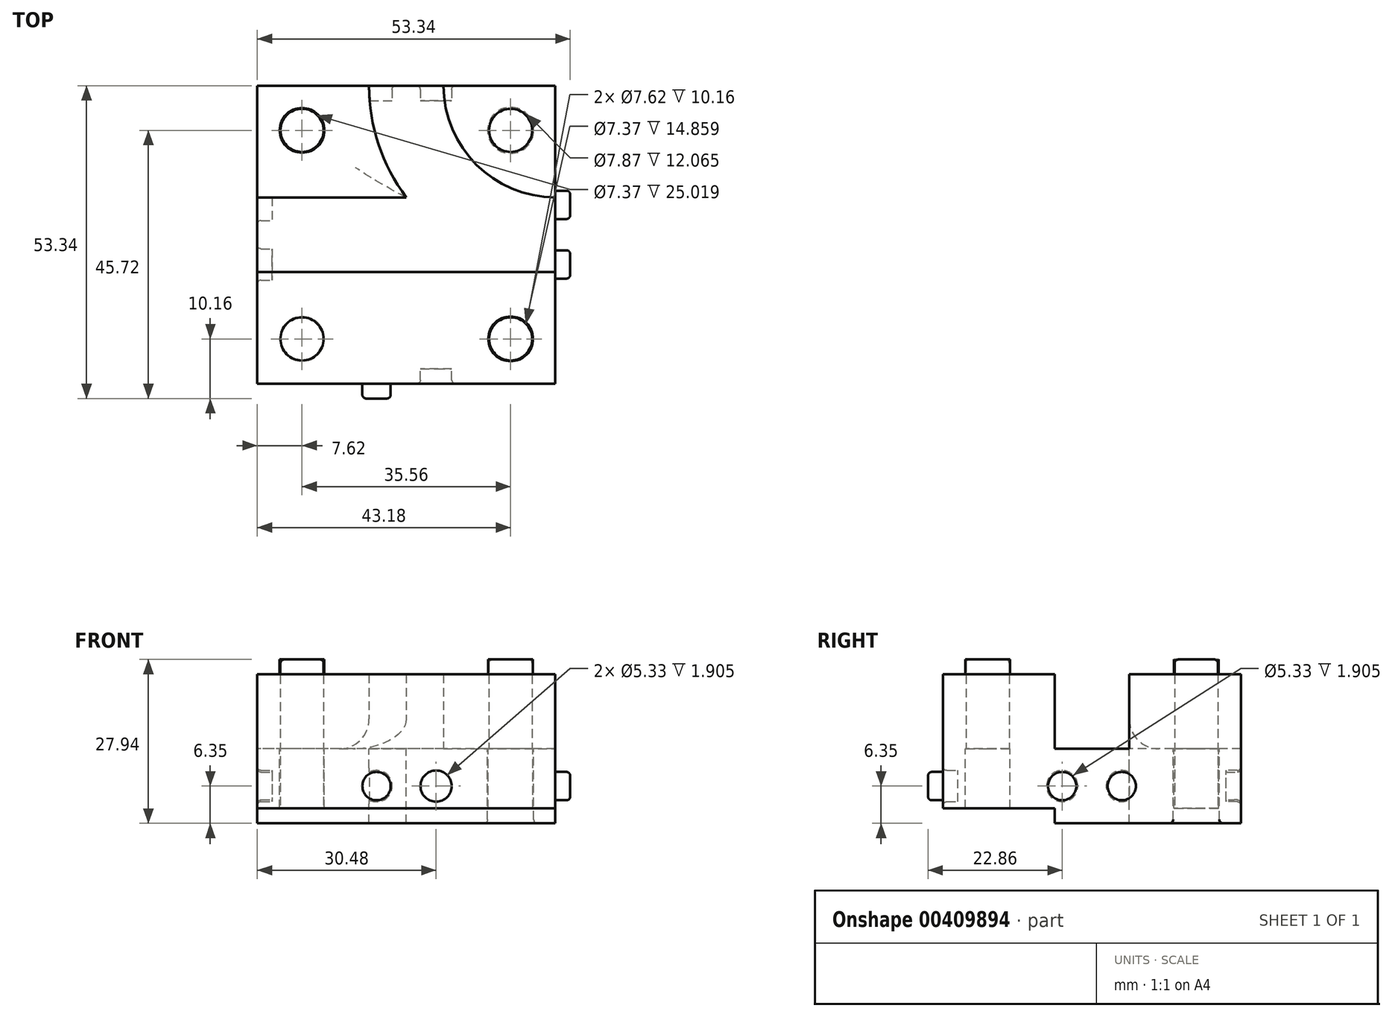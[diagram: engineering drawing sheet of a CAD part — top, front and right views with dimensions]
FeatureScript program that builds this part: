
annotation { "Feature Type Name" : "Feature", "Feature Type Description" : "" }
export const myFeature = defineFeature(function(context is Context, id is Id, definition is map)
    precondition{}
    {
        {
            var Q0;
            Q0=qCreatedBy(makeId("Top.planeOp"),FACE);
            var sketch = newSketch(context, id + "F0", { "sketchPlane" : qUnion([Q0])});
            skLineSegment(sketch, "E0.bottom", {"start": v(25.4, 25.4) * mm, "end": v(-25.4, 25.4) * mm});
            skLineSegment(sketch, "E0.top", {"start": v(25.4, -25.4) * mm, "end": v(-25.4, -25.4) * mm});
            skLineSegment(sketch, "E0.left", {"start": v(25.4, 25.4) * mm, "end": v(25.4, -25.4) * mm});
            skLineSegment(sketch, "E0.right", {"start": v(-25.4, 25.4) * mm, "end": v(-25.4, -25.4) * mm});
            skPoint(sketch, "E0.middle", {"position": v(0, 0) * mm});
            skPoint(sketch, "E1", {"position": v(17.78, 17.78) * mm});
            skCircle(sketch, "E2", {"center": v(17.78, 17.78) * mm, "radius": 3.81 * mm, "construction": true});
            skCircle(sketch, "E3.MirrorC", {"center": v(-17.78, 17.78) * mm, "radius": 3.81 * mm});
            skCircle(sketch, "E4.MirrorC", {"center": v(17.78, -17.78) * mm, "radius": 3.81 * mm});
            skCircle(sketch, "E5.MirrorC", {"center": v(-17.78, -17.78) * mm, "radius": 3.81 * mm});
            skPoint(sketch, "E6", {"position": v(25.4, 0) * mm});
            skPoint(sketch, "E7", {"position": v(-25.4, 0) * mm});
            skCircle(sketch, "E8", {"center": v(17.78, 17.78) * mm, "radius": 3.68 * mm});
            skCircle(sketch, "E9.MirrorC", {"center": v(-17.78, 17.78) * mm, "radius": 3.68 * mm});
            skCircle(sketch, "E10.MirrorC", {"center": v(-17.78, -17.78) * mm, "radius": 3.68 * mm});
            skCircle(sketch, "E11.MirrorC", {"center": v(17.78, -17.78) * mm, "radius": 3.68 * mm});
            skLineSegment(sketch, "E12", {"start": v(-25.4, 0) * mm, "end": v(25.4, 0) * mm, "construction": true});
            skPoint(sketch, "E13", {"position": v(6.35, 25.4) * mm});
            skPoint(sketch, "E14.MirrorP", {"position": v(-6.35, 25.4) * mm});
            skArc(sketch, "E15", {"start": v(6.35, 25.4) * mm, "mid": v(11.93, 11.93) * mm, "end": v(25.4, 6.35) * mm});
            skLineSegment(sketch, "E16", {"start": v(0, 25.4) * mm, "end": v(0, -25.4) * mm, "construction": true});
            skCircle(sketch, "E17", {"center": v(0, 0) * mm, "radius": 2.54 * mm, "construction": true});
            skPoint(sketch, "E18", {"position": v(0, 2.54) * mm});
            skPoint(sketch, "E19", {"position": v(0, 5.08) * mm});
            skCircle(sketch, "E20", {"center": v(0, 0) * mm, "radius": 2.41 * mm});
            skCircle(sketch, "E21", {"center": v(0, 0) * mm, "radius": 2.67 * mm});
            skPoint(sketch, "E22", {"position": v(2.41, 0) * mm});
            skPoint(sketch, "E23", {"position": v(2.67, 0) * mm});
            skLineSegment(sketch, "E24", {"start": v(2.41, 0) * mm, "end": v(2.67, 0) * mm});
            skCircle(sketch, "E25", {"center": v(17.78, 17.78) * mm, "radius": 3.94 * mm});
            skLineSegment(sketch, "E26", {"start": v(17.78, 21.46) * mm, "end": v(17.78, 21.72) * mm});
            skPoint(sketch, "E26.endSnap0", {"position": v(17.78, 21.59) * mm});
            skLineSegment(sketch, "E27", {"start": v(25.4, -6.35) * mm, "end": v(-25.4, -6.35) * mm});
            skLineSegment(sketch, "E28", {"start": v(25.4, 6.35) * mm, "end": v(0, 6.35) * mm, "construction": true});
            skLineSegment(sketch, "E29", {"start": v(0, 6.35) * mm, "end": v(-25.4, 6.35) * mm});
            skArc(sketch, "E30", {"start": v(-6.35, 25.4) * mm, "mid": v(-4.72, 15.36) * mm, "end": v(0, 6.35) * mm});
            skLineSegment(sketch, "E31", {"start": v(25.4, 6.35) * mm, "end": v(25.4, -6.35) * mm});
            skPoint(sketch, "E32", {"position": v(2.54, 0) * mm});
            skCircle(sketch, "E33", {"center": v(0, 0) * mm, "radius": 5.08 * mm});
            skLineSegment(sketch, "E34", {"start": v(17.78, 25.4) * mm, "end": v(17.78, 17.78) * mm, "construction": true});
            skLineSegment(sketch, "E35", {"start": v(17.78, 17.78) * mm, "end": v(25.4, 17.78) * mm, "construction": true});
            skSolve(sketch);
        }
        {
            var Q0;
            Q0=makeQuery(id+"F0.imprint","IMPRINT",FACE,{"disambiguationData":[TD([[makeQuery(id+"F0.imprint","IMPRINT",EDGE,{"derivedFrom":sQuery(id+"F0.wireOp",EDGE,"E3.MirrorC")}),1.0]])]});
            var Q1;
            {var subQ0=sQuery(id+"F0.wireOp",EDGE,"e8c6bd5a-b162-413f-9673-ee5317453a08.1.0");var subQ1=sQuery(id+"F0.wireOp",EDGE,"E0.right");var subQ2=makeQuery(id+"F0.imprint","INTERSECT",VERTEX,{"derivedFrom":[subQ1,subQ0]});Q1=makeQuery(id+"F0.imprint","IMPRINT",FACE,{"disambiguationData":[TD([[makeQuery(id+"F0.imprint","IMPRINT",EDGE,{"disambiguationData":[TD([[subQ2,-1.0]])],"derivedFrom":subQ1}),1.0]])]});}
            var Q2;
            Q2=makeQuery(id+"F0.imprint","IMPRINT",FACE,{"disambiguationData":[TD([[makeQuery(id+"F0.imprint","IMPRINT",EDGE,{"derivedFrom":sQuery(id+"F0.wireOp",EDGE,"E5.MirrorC")}),-1.0]])]});
            var Q3;
            Q3=makeQuery(id+"F0.imprint","IMPRINT",FACE,{"disambiguationData":[TD([[makeQuery(id+"F0.imprint","IMPRINT",EDGE,{"derivedFrom":sQuery(id+"F0.wireOp",EDGE,"E3.MirrorC")}),-1.0]])]});
            var Q4;
            Q4=makeQuery(id+"F0.imprint","IMPRINT",FACE,{"disambiguationData":[TD([[makeQuery(id+"F0.imprint","IMPRINT",EDGE,{"derivedFrom":sQuery(id+"F0.wireOp",EDGE,"E5.MirrorC")}),1.0]])]});
            var Q5;
            Q5=makeQuery(id+"F0.imprint","IMPRINT",FACE,{"disambiguationData":[TD([[makeQuery(id+"F0.imprint","IMPRINT",EDGE,{"derivedFrom":sQuery(id+"F0.wireOp",EDGE,"E4.MirrorC")}),-1.0]])]});
            var Q6;
            {var subQ0=sQuery(id+"F0.wireOp",EDGE,"E16");var subQ1=sQuery(id+"F0.wireOp",EDGE,"E0.top");var subQ2=makeQuery(id+"F0.imprint","INTERSECT",VERTEX,{"derivedFrom":[subQ1,subQ0]});Q6=makeQuery(id+"F0.imprint","IMPRINT",FACE,{"disambiguationData":[TD([[makeQuery(id+"F0.imprint","IMPRINT",EDGE,{"disambiguationData":[TD([[subQ2,-1.0]])],"derivedFrom":subQ1}),-1.0]])]});}
            var Q7;
            {var subQ0=sQuery(id+"F0.wireOp",EDGE,"E16");var subQ1=sQuery(id+"F0.wireOp",EDGE,"E0.top");var subQ2=makeQuery(id+"F0.imprint","INTERSECT",VERTEX,{"derivedFrom":[subQ1,subQ0]});Q7=makeQuery(id+"F0.imprint","IMPRINT",FACE,{"disambiguationData":[TD([[makeQuery(id+"F0.imprint","IMPRINT",EDGE,{"disambiguationData":[TD([[subQ2,1.0]])],"derivedFrom":subQ1}),-1.0]])]});}
            var Q8;
            Q8=makeQuery(id+"F0.imprint","IMPRINT",FACE,{"disambiguationData":[TD([[makeQuery(id+"F0.imprint","IMPRINT",EDGE,{"derivedFrom":sQuery(id+"F0.wireOp",EDGE,"E4.MirrorC")}),1.0]])]});
            var Q9;
            Q9=makeQuery(id+"F0.imprint","IMPRINT",FACE,{"disambiguationData":[TD([[makeQuery(id+"F0.imprint","IMPRINT",EDGE,{"derivedFrom":sQuery(id+"F0.wireOp",EDGE,"E8")}),-1.0]])]});
            var Q10;
            {var subQ5=sQuery(id+"F0.wireOp",EDGE,"E15");Q10=makeQuery(id+"F0.imprint","IMPRINT",FACE,{"disambiguationData":[TD([[makeQuery(id+"F0.imprint","IMPRINT",EDGE,{"derivedFrom":subQ5}),1.0]])]});}
            var Q11;
            {var subQ0=sQuery(id+"F0.wireOp",EDGE,"E34");var subQ1=sQuery(id+"F0.wireOp",EDGE,"E8");var subQ2=makeQuery(id+"F0.imprint","INTERSECT",VERTEX,{"derivedFrom":[subQ1,subQ0]});Q11=makeQuery(id+"F0.imprint","IMPRINT",FACE,{"disambiguationData":[TD([[makeQuery(id+"F0.imprint","IMPRINT",EDGE,{"disambiguationData":[TD([[subQ2,1.0]])],"derivedFrom":subQ1}),1.0]])]});}
            var Q12;
            {var subQ0=sQuery(id+"F0.wireOp",EDGE,"E34");var subQ1=sQuery(id+"F0.wireOp",EDGE,"E8");var subQ2=makeQuery(id+"F0.imprint","INTERSECT",VERTEX,{"derivedFrom":[subQ1,subQ0]});Q12=makeQuery(id+"F0.imprint","IMPRINT",FACE,{"disambiguationData":[TD([[makeQuery(id+"F0.imprint","IMPRINT",EDGE,{"disambiguationData":[TD([[subQ2,-1.0]])],"derivedFrom":subQ1}),1.0]])]});}
            var Q13;
            Q13=makeQuery(id+"F0.imprint","IMPRINT",FACE,{"disambiguationData":[TD([[makeQuery(id+"F0.imprint","IMPRINT",EDGE,{"derivedFrom":sQuery(id+"F0.wireOp",EDGE,"E9.MirrorC")}),-1.0]])]});
            var Q14;
            Q14=makeQuery(id+"F0.imprint","IMPRINT",FACE,{"disambiguationData":[TD([[makeQuery(id+"F0.imprint","IMPRINT",EDGE,{"derivedFrom":sQuery(id+"F0.wireOp",EDGE,"E10.MirrorC")}),1.0]])]});
            var Q15;
            Q15=makeQuery(id+"F0.imprint","IMPRINT",FACE,{"disambiguationData":[TD([[makeQuery(id+"F0.imprint","IMPRINT",EDGE,{"derivedFrom":sQuery(id+"F0.wireOp",EDGE,"E11.MirrorC")}),-1.0]])]});
            extrude(context, id + "F1", {"entities" : qUnion([Q0, Q1, Q2, Q3, Q4, Q5, Q6, Q7, Q8, Q9, Q10, Q11, Q12, Q13, Q14, Q15]), "depth" : 12.7 * mm});
        }
        {
            var Q0;
            Q0=makeQuery(id+"F0.imprint","IMPRINT",FACE,{"disambiguationData":[TD([[makeQuery(id+"F0.imprint","IMPRINT",EDGE,{"derivedFrom":sQuery(id+"F0.wireOp",EDGE,"E10.MirrorC")}),1.0]])]});
            var Q1;
            Q1=makeQuery(id+"F0.imprint","IMPRINT",FACE,{"disambiguationData":[TD([[makeQuery(id+"F0.imprint","IMPRINT",EDGE,{"derivedFrom":sQuery(id+"F0.wireOp",EDGE,"E9.MirrorC")}),-1.0]])]});
            var Q2;
            Q2=makeQuery(id+"F0.imprint","IMPRINT",FACE,{"disambiguationData":[TD([[makeQuery(id+"F0.imprint","IMPRINT",EDGE,{"derivedFrom":sQuery(id+"F0.wireOp",EDGE,"E8")}),1.0]])]});
            var Q3;
            Q3=makeQuery(id+"F0.imprint","IMPRINT",FACE,{"disambiguationData":[TD([[makeQuery(id+"F0.imprint","IMPRINT",EDGE,{"derivedFrom":sQuery(id+"F0.wireOp",EDGE,"E11.MirrorC")}),-1.0]])]});
            extrude(context, id + "F2", {"entities" : qUnion([Q0, Q1, Q2, Q3]), "operationType" : NewBodyOperationType.ADD, "depth" : 15.24 * mm});
        }
        {
            var Q0;
            {var subQ0=sQuery(id+"F0.wireOp",EDGE,"e8c6bd5a-b162-413f-9673-ee5317453a08.1.0");var subQ1=sQuery(id+"F0.wireOp",EDGE,"E0.left");var subQ2=makeQuery(id+"F0.imprint","INTERSECT",VERTEX,{"derivedFrom":[subQ1,subQ0]});Q0=makeQuery(id+"F0.imprint","IMPRINT",FACE,{"disambiguationData":[TD([[makeQuery(id+"F0.imprint","IMPRINT",EDGE,{"disambiguationData":[TD([[subQ2,-1.0]])],"derivedFrom":subQ1}),-1.0]])]});}
            var Q1;
            {var subQ0=sQuery(id+"F0.wireOp",EDGE,"abd07589-5baa-48c3-989b-ebb05b9b5cfd");var subQ1=sQuery(id+"F0.wireOp",EDGE,"E0.bottom");var subQ2=makeQuery(id+"F0.imprint","INTERSECT",VERTEX,{"derivedFrom":[subQ1,subQ0]});Q1=makeQuery(id+"F0.imprint","IMPRINT",FACE,{"disambiguationData":[TD([[makeQuery(id+"F0.imprint","IMPRINT",EDGE,{"disambiguationData":[TD([[subQ2,1.0]])],"derivedFrom":subQ1}),1.0]])]});}
            var Q2;
            {var subQ0=sQuery(id+"F0.wireOp",EDGE,"E16");var subQ1=sQuery(id+"F0.wireOp",EDGE,"E0.bottom");var subQ2=makeQuery(id+"F0.imprint","INTERSECT",VERTEX,{"derivedFrom":[subQ1,subQ0]});Q2=makeQuery(id+"F0.imprint","IMPRINT",FACE,{"disambiguationData":[TD([[makeQuery(id+"F0.imprint","IMPRINT",EDGE,{"disambiguationData":[TD([[subQ2,-1.0]])],"derivedFrom":subQ1}),1.0]])]});}
            var Q3;
            {var subQ0=sQuery(id+"F0.wireOp",EDGE,"E16");var subQ1=sQuery(id+"F0.wireOp",EDGE,"E0.bottom");var subQ2=makeQuery(id+"F0.imprint","INTERSECT",VERTEX,{"derivedFrom":[subQ1,subQ0]});Q3=makeQuery(id+"F0.imprint","IMPRINT",FACE,{"disambiguationData":[TD([[makeQuery(id+"F0.imprint","IMPRINT",EDGE,{"disambiguationData":[TD([[subQ2,1.0]])],"derivedFrom":subQ1}),1.0]])]});}
            var Q4;
            {var subQ5=sQuery(id+"F0.wireOp",EDGE,"E15");Q4=makeQuery(id+"F0.imprint","IMPRINT",FACE,{"disambiguationData":[TD([[makeQuery(id+"F0.imprint","IMPRINT",EDGE,{"derivedFrom":subQ5}),-1.0]])]});}
            var Q5;
            {var subQ0=sQuery(id+"F0.wireOp",EDGE,"E12");var subQ1=sQuery(id+"F0.wireOp",EDGE,"E0.left");var subQ2=makeQuery(id+"F0.imprint","INTERSECT",VERTEX,{"derivedFrom":[subQ1,subQ0]});Q5=makeQuery(id+"F0.imprint","IMPRINT",FACE,{"disambiguationData":[TD([[makeQuery(id+"F0.imprint","IMPRINT",EDGE,{"disambiguationData":[TD([[subQ2,1.0]])],"derivedFrom":subQ1}),-1.0]])]});}
            var Q6;
            {var subQ1=sQuery(id+"F0.wireOp",EDGE,"E12");var subQ7=sQuery(id+"F0.wireOp",EDGE,"E0.left");var subQ8=makeQuery(id+"F0.imprint","INTERSECT",VERTEX,{"derivedFrom":[subQ7,subQ1]});Q6=makeQuery(id+"F0.imprint","IMPRINT",FACE,{"disambiguationData":[TD([[makeQuery(id+"F0.imprint","IMPRINT",EDGE,{"disambiguationData":[TD([[subQ8,-1.0]])],"derivedFrom":subQ7}),-1.0]])]});}
            var Q7;
            Q7=makeQuery(id+"F0.imprint","IMPRINT",FACE,{"disambiguationData":[TD([[makeQuery(id+"F0.imprint","IMPRINT",EDGE,{"derivedFrom":sQuery(id+"F0.wireOp",EDGE,"E20")}),1.0]])]});
            var Q8;
            Q8=makeQuery(id+"F0.imprint","IMPRINT",FACE,{"disambiguationData":[TD([[makeQuery(id+"F0.imprint","IMPRINT",EDGE,{"derivedFrom":sQuery(id+"F0.wireOp",EDGE,"E20")}),-1.0]])]});
            var Q9;
            {var subQ11=sQuery(id+"F0.wireOp",EDGE,"E0.top");Q9=makeQuery(id+"F0.imprint","IMPRINT",FACE,{"disambiguationData":[TD([[makeQuery(id+"F0.imprint","IMPRINT",EDGE,{"derivedFrom":subQ11}),-1.0]])]});}
            var Q10;
            Q10=makeQuery(id+"F0.imprint","IMPRINT",FACE,{"disambiguationData":[TD([[makeQuery(id+"F0.imprint","IMPRINT",EDGE,{"derivedFrom":sQuery(id+"F0.wireOp",EDGE,"E3.MirrorC")}),1.0]])]});
            var Q11;
            Q11=makeQuery(id+"F0.imprint","IMPRINT",FACE,{"disambiguationData":[TD([[makeQuery(id+"F0.imprint","IMPRINT",EDGE,{"derivedFrom":sQuery(id+"F0.wireOp",EDGE,"E21")}),-1.0]])]});
            extrude(context, id + "F3", {"entities" : qUnion([Q0, Q1, Q2, Q3, Q4, Q5, Q6, Q7, Q8, Q9, Q10, Q11]), "operationType" : NewBodyOperationType.ADD, "oppositeDirection" : true, "depth" : 12.7 * mm});
        }
        {
            var Q0;
            Q0=makeQuery(id+"F0.imprint","IMPRINT",FACE,{"disambiguationData":[TD([[makeQuery(id+"F0.imprint","IMPRINT",EDGE,{"derivedFrom":sQuery(id+"F0.wireOp",EDGE,"E11.MirrorC")}),-1.0]])]});
            var Q1;
            Q1=makeQuery(id+"F0.imprint","IMPRINT",FACE,{"disambiguationData":[TD([[makeQuery(id+"F0.imprint","IMPRINT",EDGE,{"derivedFrom":sQuery(id+"F0.wireOp",EDGE,"E5.MirrorC")}),1.0]])]});
            var Q2;
            Q2=makeQuery(id+"F0.imprint","IMPRINT",FACE,{"disambiguationData":[TD([[makeQuery(id+"F0.imprint","IMPRINT",EDGE,{"derivedFrom":sQuery(id+"F0.wireOp",EDGE,"E10.MirrorC")}),1.0]])]});
            var Q3;
            Q3=makeQuery(id+"F0.imprint","IMPRINT",FACE,{"disambiguationData":[TD([[makeQuery(id+"F0.imprint","IMPRINT",EDGE,{"derivedFrom":sQuery(id+"F0.wireOp",EDGE,"E4.MirrorC")}),-1.0]])]});
            var Q4;
            Q4=makeQuery(id+"F0.imprint","IMPRINT",FACE,{"disambiguationData":[TD([[makeQuery(id+"F0.imprint","IMPRINT",EDGE,{"derivedFrom":sQuery(id+"F0.wireOp",EDGE,"E8")}),-1.0]])]});
            var Q5;
            Q5=makeQuery(id+"F0.imprint","IMPRINT",FACE,{"disambiguationData":[TD([[makeQuery(id+"F0.imprint","IMPRINT",EDGE,{"derivedFrom":sQuery(id+"F0.wireOp",EDGE,"E8")}),1.0]])]});
            var Q6;
            Q6=makeQuery(id+"F0.imprint","IMPRINT",FACE,{"disambiguationData":[TD([[makeQuery(id+"F0.imprint","IMPRINT",EDGE,{"derivedFrom":sQuery(id+"F0.wireOp",EDGE,"E3.MirrorC")}),-1.0]])]});
            var Q7;
            Q7=makeQuery(id+"F0.imprint","IMPRINT",FACE,{"disambiguationData":[TD([[makeQuery(id+"F0.imprint","IMPRINT",EDGE,{"derivedFrom":sQuery(id+"F0.wireOp",EDGE,"E9.MirrorC")}),-1.0]])]});
            extrude(context, id + "F4", {"entities" : qUnion([Q0, Q1, Q2, Q3, Q4, Q5, Q6, Q7]), "operationType" : NewBodyOperationType.REMOVE, "oppositeDirection" : true, "depth" : 12.7 * mm, "hasSecondDirection" : true, "secondDirectionOppositeDirection" : true, "secondDirectionDepth" : 10.16 * mm});
        }
        {
            var Q0;
            Q0=qCreatedBy(makeId("Right.planeOp"),FACE);
            var sketch = newSketch(context, id + "F5", { "sketchPlane" : qUnion([Q0])});
            skLineSegment(sketch, "E36", {"start": v(-25.4, 12.7) * mm, "end": v(-25.4, -12.7) * mm, "construction": true});
            skLineSegment(sketch, "E37", {"start": v(25.4, 0) * mm, "end": v(25.4, -12.7) * mm, "construction": true});
            skPoint(sketch, "E38", {"position": v(-25.4, 0) * mm});
            skPoint(sketch, "E39", {"position": v(-25.4, -6.35) * mm});
            skPoint(sketch, "E40", {"position": v(25.4, -6.35) * mm});
            skLineSegment(sketch, "E41", {"start": v(-2.41, 0) * mm, "end": v(-2.67, 0) * mm, "construction": true});
            skLineSegment(sketch, "E42", {"start": v(2.67, 0) * mm, "end": v(2.41, 0) * mm, "construction": true});
            skPoint(sketch, "E43", {"position": v(-5.08, -6.35) * mm});
            skPoint(sketch, "E44", {"position": v(-2.67, -6.35) * mm});
            skPoint(sketch, "E45", {"position": v(-2.41, -6.35) * mm});
            skPoint(sketch, "E46", {"position": v(2.41, -6.35) * mm});
            skPoint(sketch, "E47", {"position": v(2.67, -6.35) * mm});
            skPoint(sketch, "E48", {"position": v(5.08, -6.35) * mm});
            skCircle(sketch, "E49", {"center": v(-5.08, -6.35) * mm, "radius": 2.41 * mm});
            skCircle(sketch, "E50", {"center": v(-5.08, -6.35) * mm, "radius": 2.67 * mm});
            skCircle(sketch, "E51", {"center": v(5.08, -6.35) * mm, "radius": 2.41 * mm});
            skCircle(sketch, "E52", {"center": v(5.08, -6.35) * mm, "radius": 2.67 * mm});
            skLineSegment(sketch, "E53", {"start": v(-2.67, 0) * mm, "end": v(-5.08, 0) * mm});
            skLineSegment(sketch, "E54", {"start": v(5.08, 0) * mm, "end": v(2.67, 0) * mm});
            skSolve(sketch);
        }
        {
            var Q0;
            Q0=qCreatedBy(makeId("Front.planeOp"),FACE);
            var sketch = newSketch(context, id + "F6", { "sketchPlane" : qUnion([Q0])});
            skLineSegment(sketch, "E55", {"start": v(-25.4, -12.7) * mm, "end": v(-25.4, 12.7) * mm, "construction": true});
            skLineSegment(sketch, "E56", {"start": v(25.4, -12.7) * mm, "end": v(25.4, 0) * mm, "construction": true});
            skPoint(sketch, "E57", {"position": v(25.4, -6.35) * mm});
            skPoint(sketch, "E58", {"position": v(-25.4, 0) * mm});
            skPoint(sketch, "E59", {"position": v(-25.4, -6.35) * mm});
            skLineSegment(sketch, "E60", {"start": v(-2.41, 0) * mm, "end": v(-2.67, 0) * mm, "construction": true});
            skLineSegment(sketch, "E61", {"start": v(2.67, 0) * mm, "end": v(2.41, 0) * mm, "construction": true});
            skPoint(sketch, "E62", {"position": v(5.08, -6.35) * mm});
            skPoint(sketch, "E63", {"position": v(2.67, -6.35) * mm});
            skPoint(sketch, "E64", {"position": v(2.41, -6.35) * mm});
            skPoint(sketch, "E65", {"position": v(-2.41, -6.35) * mm});
            skPoint(sketch, "E66", {"position": v(-2.67, -6.35) * mm});
            skPoint(sketch, "E67", {"position": v(-5.08, -6.35) * mm});
            skCircle(sketch, "E68", {"center": v(5.08, -6.35) * mm, "radius": 2.41 * mm});
            skCircle(sketch, "E69", {"center": v(5.08, -6.35) * mm, "radius": 2.67 * mm});
            skCircle(sketch, "E70", {"center": v(-5.08, -6.35) * mm, "radius": 2.67 * mm});
            skCircle(sketch, "E71", {"center": v(-5.08, -6.35) * mm, "radius": 2.41 * mm});
            skLineSegment(sketch, "E72", {"start": v(-2.67, 0) * mm, "end": v(-5.08, 0) * mm});
            skLineSegment(sketch, "E73", {"start": v(5.08, 0) * mm, "end": v(2.67, 0) * mm});
            skSolve(sketch);
        }
        {
            var Q0;
            Q0=makeQuery(id+"F6.imprint","IMPRINT",FACE,{"disambiguationData":[TD([[makeQuery(id+"F6.imprint","IMPRINT",EDGE,{"derivedFrom":sQuery(id+"F6.wireOp",EDGE,"E71")}),1.0]])]});
            extrude(context, id + "F7", {"entities" : qUnion([Q0]), "operationType" : NewBodyOperationType.ADD, "depth" : 27.94 * mm, "hasSecondDirection" : true, "secondDirectionOppositeDirection" : false, "secondDirectionDepth" : 22.86 * mm});
        }
        {
            var Q0;
            Q0=makeQuery(id+"F6.imprint","IMPRINT",FACE,{"disambiguationData":[TD([[makeQuery(id+"F6.imprint","IMPRINT",EDGE,{"derivedFrom":sQuery(id+"F6.wireOp",EDGE,"E71")}),1.0]])]});
            var Q1;
            Q1=makeQuery(id+"F6.imprint","IMPRINT",FACE,{"disambiguationData":[TD([[makeQuery(id+"F6.imprint","IMPRINT",EDGE,{"derivedFrom":sQuery(id+"F6.wireOp",EDGE,"E68")}),1.0]])]});
            var Q2;
            Q2=makeQuery(id+"F6.imprint","IMPRINT",FACE,{"disambiguationData":[TD([[makeQuery(id+"F6.imprint","IMPRINT",EDGE,{"derivedFrom":sQuery(id+"F6.wireOp",EDGE,"E70")}),1.0]])]});
            var Q3;
            Q3=makeQuery(id+"F6.imprint","IMPRINT",FACE,{"disambiguationData":[TD([[makeQuery(id+"F6.imprint","IMPRINT",EDGE,{"derivedFrom":sQuery(id+"F6.wireOp",EDGE,"E68")}),-1.0]])]});
            extrude(context, id + "F8", {"entities" : qUnion([Q0, Q1, Q2, Q3]), "operationType" : NewBodyOperationType.REMOVE, "oppositeDirection" : true, "depth" : 27.94 * mm, "hasSecondDirection" : true, "secondDirectionOppositeDirection" : true, "secondDirectionDepth" : 22.86 * mm});
        }
        {
            var Q0;
            Q0=makeQuery(id+"F5.imprint","IMPRINT",FACE,{"disambiguationData":[TD([[makeQuery(id+"F5.imprint","IMPRINT",EDGE,{"derivedFrom":sQuery(id+"F5.wireOp",EDGE,"E49")}),1.0]])]});
            var Q1;
            Q1=makeQuery(id+"F5.imprint","IMPRINT",FACE,{"disambiguationData":[TD([[makeQuery(id+"F5.imprint","IMPRINT",EDGE,{"derivedFrom":sQuery(id+"F5.wireOp",EDGE,"E51")}),1.0]])]});
            extrude(context, id + "F9", {"entities" : qUnion([Q0, Q1]), "operationType" : NewBodyOperationType.ADD, "depth" : 27.94 * mm, "hasSecondDirection" : true, "secondDirectionOppositeDirection" : false, "secondDirectionDepth" : 22.86 * mm});
        }
        {
            var Q0;
            Q0=makeQuery(id+"F5.imprint","IMPRINT",FACE,{"disambiguationData":[TD([[makeQuery(id+"F5.imprint","IMPRINT",EDGE,{"derivedFrom":sQuery(id+"F5.wireOp",EDGE,"E49")}),-1.0]])]});
            var Q1;
            Q1=makeQuery(id+"F5.imprint","IMPRINT",FACE,{"disambiguationData":[TD([[makeQuery(id+"F5.imprint","IMPRINT",EDGE,{"derivedFrom":sQuery(id+"F5.wireOp",EDGE,"E49")}),1.0]])]});
            var Q2;
            Q2=makeQuery(id+"F5.imprint","IMPRINT",FACE,{"disambiguationData":[TD([[makeQuery(id+"F5.imprint","IMPRINT",EDGE,{"derivedFrom":sQuery(id+"F5.wireOp",EDGE,"E51")}),1.0]])]});
            var Q3;
            Q3=makeQuery(id+"F5.imprint","IMPRINT",FACE,{"disambiguationData":[TD([[makeQuery(id+"F5.imprint","IMPRINT",EDGE,{"derivedFrom":sQuery(id+"F5.wireOp",EDGE,"E51")}),-1.0]])]});
            extrude(context, id + "F10", {"entities" : qUnion([Q0, Q1, Q2, Q3]), "operationType" : NewBodyOperationType.REMOVE, "oppositeDirection" : true, "depth" : 27.94 * mm, "hasSecondDirection" : true, "secondDirectionOppositeDirection" : true, "secondDirectionDepth" : 22.86 * mm});
        }
        {
            var Q0;
            Q0=makeQuery(id+"F6.imprint","IMPRINT",FACE,{"disambiguationData":[TD([[makeQuery(id+"F6.imprint","IMPRINT",EDGE,{"derivedFrom":sQuery(id+"F6.wireOp",EDGE,"E68")}),1.0]])]});
            var Q1;
            Q1=makeQuery(id+"F6.imprint","IMPRINT",FACE,{"disambiguationData":[TD([[makeQuery(id+"F6.imprint","IMPRINT",EDGE,{"derivedFrom":sQuery(id+"F6.wireOp",EDGE,"E68")}),-1.0]])]});
            extrude(context, id + "F11", {"entities" : qUnion([Q0, Q1]), "operationType" : NewBodyOperationType.REMOVE, "depth" : 27.94 * mm, "hasSecondDirection" : true, "secondDirectionOppositeDirection" : false, "secondDirectionDepth" : 22.86 * mm});
        }
        {
            var Q0;
            Q0=makeQuery(id+"F1.opExtrude","CAP_EDGE",EDGE,{"disambiguationData":[OSD([sQuery(id+"F0.wireOp",EDGE,"E15")])],"isStart":true});
            var Q1;
            Q1=makeQuery(id+"F1.opExtrude","CAP_EDGE",EDGE,{"disambiguationData":[OSD([sQuery(id+"F0.wireOp",EDGE,"E30")])],"isStart":true});
            var Q2;
            Q2=makeQuery(id+"F1.opExtrude","CAP_EDGE",EDGE,{"disambiguationData":[OSD([sQuery(id+"F0.wireOp",EDGE,"E27")])],"isStart":true});
            var Q3;
            Q3=makeQuery(id+"F1.opExtrude","CAP_EDGE",EDGE,{"disambiguationData":[OSD([sQuery(id+"F0.wireOp",EDGE,"E29")])],"isStart":true});
            fillet(context, id + "F12", {"entities" : qUnion([Q0, Q1, Q2, Q3]), "radius" : 5.08 * mm, "tangentPropagation" : true, "allowEdgeOverflow" : false});
        }
        {
            var Q0;
            Q0=makeQuery(id+"F2.opExtrude","CAP_EDGE",EDGE,{"disambiguationData":[OSD([sQuery(id+"F0.wireOp",EDGE,"E11.MirrorC")])],"isStart":false});
            var Q1;
            Q1=makeQuery(id+"F2.opExtrude","CAP_EDGE",EDGE,{"disambiguationData":[OSD([sQuery(id+"F0.wireOp",EDGE,"E10.MirrorC")])],"isStart":false});
            var Q2;
            Q2=makeQuery(id+"F2.opExtrude","CAP_EDGE",EDGE,{"disambiguationData":[OSD([sQuery(id+"F0.wireOp",EDGE,"E9.MirrorC")])],"isStart":false});
            var Q3;
            Q3=makeQuery(id+"F2.opExtrude","CAP_EDGE",EDGE,{"disambiguationData":[OSD([sQuery(id+"F0.wireOp",EDGE,"E8")])],"isStart":false});
            var Q4;
            Q4=makeQuery(id+"F7.opExtrude","CAP_EDGE",EDGE,{"disambiguationData":[OSD([sQuery(id+"F6.wireOp",EDGE,"E71")])],"isStart":false});
            var Q5;
            Q5=makeQuery(id+"F3.opExtrude","CAP_EDGE",EDGE,{"disambiguationData":[OSD([sQuery(id+"F0.wireOp",EDGE,"E5.MirrorC")])],"isStart":false});
            var Q6;
            Q6=makeQuery(id+"F3.opExtrude","CAP_EDGE",EDGE,{"disambiguationData":[OSD([sQuery(id+"F0.wireOp",EDGE,"E4.MirrorC")])],"isStart":false});
            var Q7;
            Q7=makeQuery(id+"F4.opExtrude","CAP_EDGE",EDGE,{"disambiguationData":[OSD([sQuery(id+"F0.wireOp",EDGE,"E3.MirrorC")])],"isStart":false});
            var Q8;
            Q8=makeQuery(id+"F3.opExtrude","CAP_EDGE",EDGE,{"disambiguationData":[OSD([sQuery(id+"F0.wireOp",EDGE,"E25")])],"isStart":false});
            var Q9;
            {var subQ0=sQuery(id+"F0.wireOp",EDGE,"E0.right");Q9=makeQuery(id+"F10.boolean.opBoolean","INTERSECT",EDGE,{"derivedFrom":[makeQuery(id+"FVeaqIvGeaTVGBi_11.opBoolean","MERGE",FACE,{"derivedFrom":[makeQuery(id+"F1.opExtrude","SWEPT_FACE",FACE,{"disambiguationData":[OSD([subQ0])]}),makeQuery(id+"F3.opExtrude","SWEPT_FACE",FACE,{"disambiguationData":[OSD([subQ0])]})]}),makeQuery(id+"F10.opExtrude","SWEPT_FACE",FACE,{"disambiguationData":[OSD([sQuery(id+"F5.wireOp",EDGE,"E50")])]})]});}
            var Q10;
            {var subQ0=sQuery(id+"F0.wireOp",EDGE,"E0.top");Q10=makeQuery(id+"F11.boolean.opBoolean","INTERSECT",EDGE,{"derivedFrom":[makeQuery(id+"FVeaqIvGeaTVGBi_11.opBoolean","MERGE",FACE,{"derivedFrom":[makeQuery(id+"F1.opExtrude","SWEPT_FACE",FACE,{"disambiguationData":[OSD([subQ0])]}),makeQuery(id+"F3.opExtrude","SWEPT_FACE",FACE,{"disambiguationData":[OSD([subQ0])]})]}),makeQuery(id+"F11.opExtrude","SWEPT_FACE",FACE,{"disambiguationData":[OSD([sQuery(id+"F6.wireOp",EDGE,"E69")])]})]});}
            var Q11;
            Q11=makeQuery(id+"F9.opExtrude","CAP_EDGE",EDGE,{"disambiguationData":[OSD([sQuery(id+"F5.wireOp",EDGE,"E51")])],"isStart":false});
            var Q12;
            Q12=makeQuery(id+"F9.opExtrude","CAP_EDGE",EDGE,{"disambiguationData":[OSD([sQuery(id+"F5.wireOp",EDGE,"E49")])],"isStart":false});
            var Q13;
            {var subQ0=sQuery(id+"F0.wireOp",EDGE,"lMXQf7WU-VQvn-eUw7-3v8j-XpuHpQXpMMjl");var subQ1=sQuery(id+"F0.wireOp",EDGE,"E0.bottom");Q13=makeQuery(id+"F8.boolean.opBoolean","INTERSECT",EDGE,{"derivedFrom":[makeQuery(id+"FVeaqIvGeaTVGBi_11.opBoolean","MERGE",FACE,{"derivedFrom":[makeQuery(id+"F1.opExtrude","SWEPT_FACE",FACE,{"disambiguationData":[OSD([subQ1,subQ0])]}),makeQuery(id+"F1.opExtrude","SWEPT_FACE",FACE,{"disambiguationData":[OSD([subQ1])]}),makeQuery(id+"F3.opExtrude","SWEPT_FACE",FACE,{"disambiguationData":[OSD([subQ1,subQ0])]})]}),makeQuery(id+"F8.opExtrude","SWEPT_FACE",FACE,{"disambiguationData":[OSD([sQuery(id+"F6.wireOp",EDGE,"E69")])]})]});}
            var Q14;
            {var subQ0=sQuery(id+"F0.wireOp",EDGE,"lMXQf7WU-VQvn-eUw7-3v8j-XpuHpQXpMMjl");var subQ1=sQuery(id+"F0.wireOp",EDGE,"E0.bottom");Q14=makeQuery(id+"F8.boolean.opBoolean","INTERSECT",EDGE,{"derivedFrom":[makeQuery(id+"FVeaqIvGeaTVGBi_11.opBoolean","MERGE",FACE,{"derivedFrom":[makeQuery(id+"F1.opExtrude","SWEPT_FACE",FACE,{"disambiguationData":[OSD([subQ1,subQ0])]}),makeQuery(id+"F1.opExtrude","SWEPT_FACE",FACE,{"disambiguationData":[OSD([subQ1])]}),makeQuery(id+"F3.opExtrude","SWEPT_FACE",FACE,{"disambiguationData":[OSD([subQ1,subQ0])]})]}),makeQuery(id+"F8.opExtrude","SWEPT_FACE",FACE,{"disambiguationData":[OSD([sQuery(id+"F6.wireOp",EDGE,"E70")])]})]});}
            var Q15;
            {var subQ0=sQuery(id+"F0.wireOp",EDGE,"E0.right");Q15=makeQuery(id+"F10.boolean.opBoolean","INTERSECT",EDGE,{"derivedFrom":[makeQuery(id+"FVeaqIvGeaTVGBi_11.opBoolean","MERGE",FACE,{"derivedFrom":[makeQuery(id+"F1.opExtrude","SWEPT_FACE",FACE,{"disambiguationData":[OSD([subQ0]),TDD([makeQuery(id+"F0.imprint","IMPRINT",EDGE,{"disambiguationData":[TD([[makeQuery(id+"F0.imprint","INTERSECT",VERTEX,{"derivedFrom":[sQuery(id+"F0.wireOp",EDGE,"E0.bottom"),subQ0]}),-1.0]])],"derivedFrom":subQ0})])]}),makeQuery(id+"F1.opExtrude","SWEPT_FACE",FACE,{"disambiguationData":[OSD([subQ0]),TDD([makeQuery(id+"F0.imprint","IMPRINT",EDGE,{"disambiguationData":[TD([[makeQuery(id+"F0.imprint","INTERSECT",VERTEX,{"derivedFrom":[sQuery(id+"F0.wireOp",EDGE,"E0.top"),subQ0]}),1.0]])],"derivedFrom":subQ0})])]}),makeQuery(id+"F3.opExtrude","SWEPT_FACE",FACE,{"disambiguationData":[OSD([subQ0])]})]}),makeQuery(id+"F10.opExtrude","SWEPT_FACE",FACE,{"disambiguationData":[OSD([sQuery(id+"F5.wireOp",EDGE,"E52")])]})]});}
            fillet(context, id + "F13", {"entities" : qUnion([Q0, Q1, Q2, Q3, Q4, Q5, Q6, Q7, Q8, Q9, Q10, Q11, Q12, Q13, Q14, Q15]), "radius" : 0.64 * mm, "tangentPropagation" : true, "allowEdgeOverflow" : false});
        }
    });
